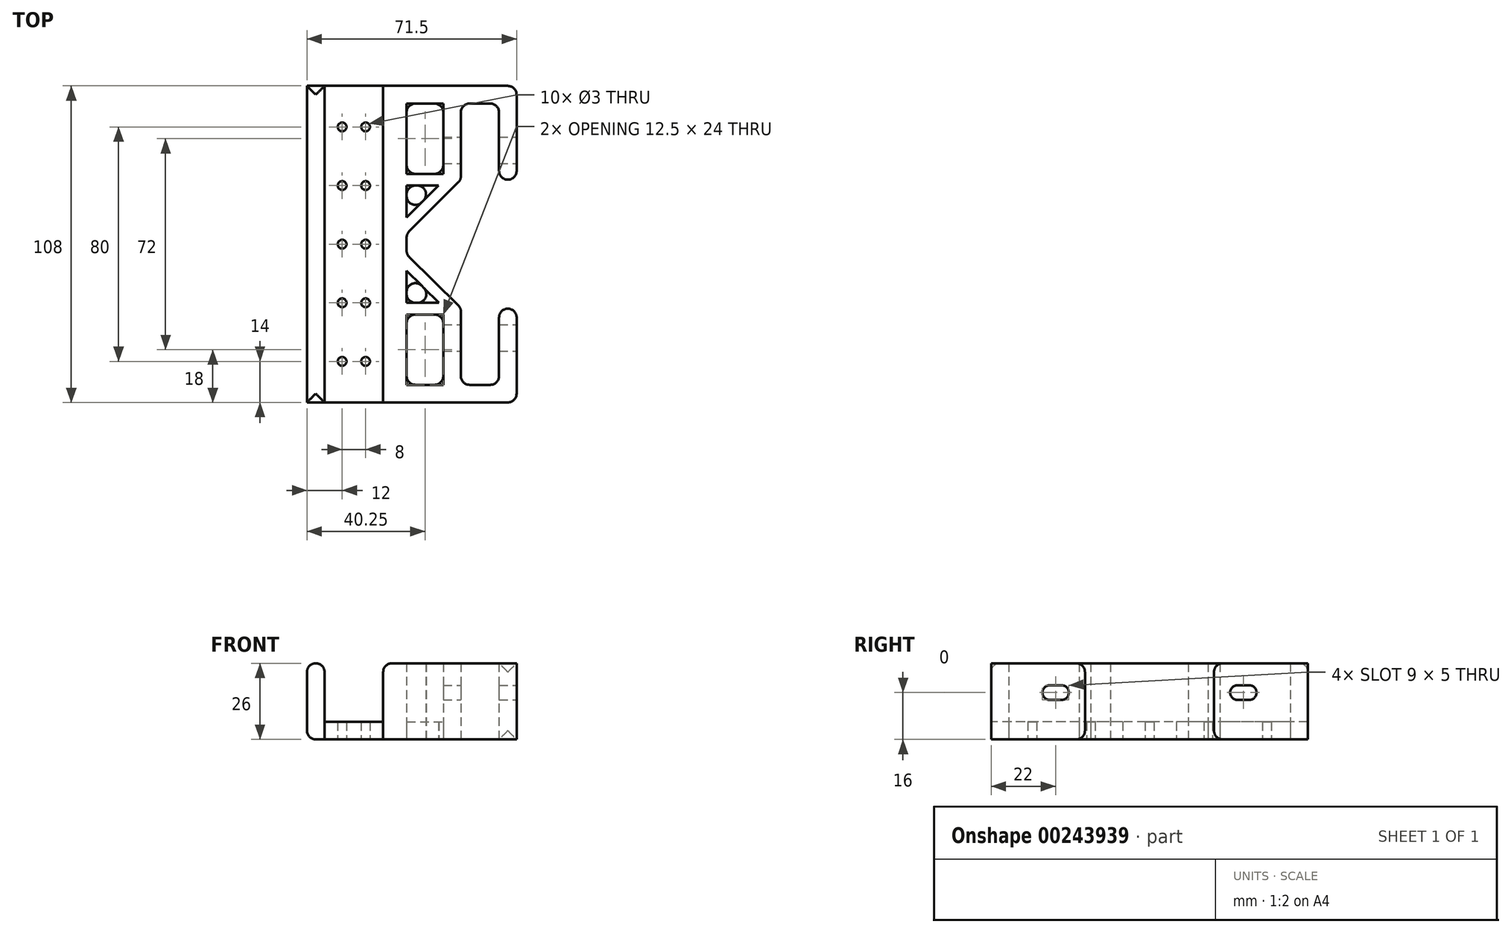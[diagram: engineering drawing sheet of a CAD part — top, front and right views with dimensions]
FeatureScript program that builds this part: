
annotation { "Feature Type Name" : "Feature", "Feature Type Description" : "" }
export const myFeature = defineFeature(function(context is Context, id is Id, definition is map)
    precondition{}
    {
        {
            var Q0;
            Q0=qCreatedBy(makeId("Top.planeOp"),FACE);
            var sketch = newSketch(context, id + "F0", { "sketchPlane" : qUnion([Q0])});
            skLineSegment(sketch, "E0", {"start": v(0, 0) * mm, "end": v(50, 0) * mm, "construction": true});
            skLineSegment(sketch, "E1.0", {"start": v(0, -30) * mm, "end": v(50, -30) * mm, "construction": true});
            skLineSegment(sketch, "E2.0", {"start": v(0, 30) * mm, "end": v(50, 30) * mm, "construction": true});
            skLineSegment(sketch, "E3", {"start": v(0, 48) * mm, "end": v(0, 24) * mm});
            skLineSegment(sketch, "E4.0", {"start": v(25, 30) * mm, "end": v(25, -30) * mm, "construction": true});
            skLineSegment(sketch, "E5.0", {"start": v(0, -48) * mm, "end": v(12.5, -48) * mm});
            skLineSegment(sketch, "E6.0", {"start": v(0, 48) * mm, "end": v(12.5, 48) * mm});
            skLineSegment(sketch, "E7.0", {"start": v(18.5, 48) * mm, "end": v(18.5, 22) * mm});
            skLineSegment(sketch, "E8.0", {"start": v(31.5, 48) * mm, "end": v(31.5, 22) * mm});
            skLineSegment(sketch, "E9.trimOffspring", {"start": v(18.5, -21.75) * mm, "end": v(18.5, -48) * mm});
            skLineSegment(sketch, "E10.trimOffspring", {"start": v(31.5, -22) * mm, "end": v(31.5, -48) * mm});
            skLineSegment(sketch, "E11", {"start": v(25, 21) * mm, "end": v(4, 0) * mm, "construction": true});
            skLineSegment(sketch, "E12", {"start": v(25, -21) * mm, "end": v(4, 0) * mm, "construction": true});
            skLineSegment(sketch, "E13", {"start": v(25, -21) * mm, "end": v(46, 0) * mm, "construction": true});
            skLineSegment(sketch, "E14", {"start": v(46, 0) * mm, "end": v(25, 21) * mm, "construction": true});
            skLineSegment(sketch, "E15.trimOffspring", {"start": v(31.5, 22) * mm, "end": v(37.5, 22) * mm});
            skLineSegment(sketch, "E16.trimOffspring", {"start": v(31.5, -22) * mm, "end": v(37.5, -22) * mm});
            skLineSegment(sketch, "E17", {"start": v(0, 3.5) * mm, "end": v(18.5, 22) * mm});
            skLineSegment(sketch, "E18", {"start": v(0, -3.5) * mm, "end": v(18.5, -21.75) * mm});
            skLineSegment(sketch, "E19.0", {"start": v(37.5, -22) * mm, "end": v(37.5, -54) * mm});
            skLineSegment(sketch, "E20.0", {"start": v(-34, -54) * mm, "end": v(37.5, -54) * mm});
            skLineSegment(sketch, "E21.0", {"start": v(37.5, 54) * mm, "end": v(37.5, 22) * mm});
            skLineSegment(sketch, "E22.0", {"start": v(-34, 54) * mm, "end": v(37.5, 54) * mm});
            skLineSegment(sketch, "E23.0", {"start": v(-8, 54) * mm, "end": v(-8, -54) * mm});
            skLineSegment(sketch, "E24.0", {"start": v(12.5, 48) * mm, "end": v(12.5, 24) * mm});
            skLineSegment(sketch, "E25.0", {"start": v(12.5, -24) * mm, "end": v(12.5, -48) * mm});
            skLineSegment(sketch, "E26.0", {"start": v(0, -9.12) * mm, "end": v(11.03, -20) * mm});
            skLineSegment(sketch, "E27.0", {"start": v(0, 9.16) * mm, "end": v(10.84, 20) * mm});
            skLineSegment(sketch, "E28.trimOffspring", {"start": v(18.5, 48) * mm, "end": v(31.5, 48) * mm});
            skLineSegment(sketch, "E29.trimOffspring", {"start": v(18.5, -48) * mm, "end": v(31.5, -48) * mm});
            skLineSegment(sketch, "E30.0", {"start": v(0, 20) * mm, "end": v(10.84, 20) * mm});
            skLineSegment(sketch, "E31.0", {"start": v(0, 24) * mm, "end": v(12.5, 24) * mm});
            skLineSegment(sketch, "E32.0", {"start": v(0, -20) * mm, "end": v(11.03, -20) * mm});
            skLineSegment(sketch, "E33.0", {"start": v(0, -24) * mm, "end": v(12.5, -24) * mm});
            skLineSegment(sketch, "E34.trimOffspring", {"start": v(0, 20) * mm, "end": v(0, 9.16) * mm});
            skLineSegment(sketch, "E35.trimOffspring", {"start": v(0, -24) * mm, "end": v(0, -48) * mm});
            skLineSegment(sketch, "E36.trimOffspring", {"start": v(0, 3.5) * mm, "end": v(0, -3.5) * mm});
            skLineSegment(sketch, "E37.trimOffspring", {"start": v(0, -9.12) * mm, "end": v(0, -20) * mm});
            skLineSegment(sketch, "E38.0", {"start": v(-28, 54) * mm, "end": v(-28, -54) * mm});
            skLineSegment(sketch, "E39.0", {"start": v(-34, 54) * mm, "end": v(-34, -54) * mm});
            skLineSegment(sketch, "E40.0", {"start": v(-28, 0) * mm, "end": v(-8, 0) * mm, "construction": true});
            skLineSegment(sketch, "E41.0", {"start": v(-14, 54) * mm, "end": v(-14, 40) * mm, "construction": true});
            skCircle(sketch, "E42", {"center": v(-22, 40) * mm, "radius": 1.5 * mm});
            skCircle(sketch, "E43", {"center": v(-14, 40) * mm, "radius": 1.5 * mm});
            skCircle(sketch, "E44", {"center": v(-22, 20) * mm, "radius": 1.5 * mm});
            skCircle(sketch, "E45", {"center": v(-14, 20) * mm, "radius": 1.5 * mm});
            skCircle(sketch, "E46", {"center": v(-22, 0) * mm, "radius": 1.5 * mm});
            skCircle(sketch, "E47", {"center": v(-14, 0) * mm, "radius": 1.5 * mm});
            skCircle(sketch, "E48", {"center": v(-22, -20) * mm, "radius": 1.5 * mm});
            skCircle(sketch, "E49", {"center": v(-14, -20) * mm, "radius": 1.5 * mm});
            skCircle(sketch, "E50", {"center": v(-22, -40) * mm, "radius": 1.5 * mm});
            skCircle(sketch, "E51", {"center": v(-14, -40) * mm, "radius": 1.5 * mm});
            skSolve(sketch);
        }
        {
            var Q0;
            Q0=makeQuery(id+"F0.imprint","IMPRINT",FACE,{"disambiguationData":[TD([[makeQuery(id+"F0.imprint","IMPRINT",EDGE,{"derivedFrom":sQuery(id+"F0.wireOp",EDGE,"E5.0")}),1.0]])]});
            var Q1;
            Q1=makeQuery(id+"F0.imprint","IMPRINT",FACE,{"disambiguationData":[TD([[makeQuery(id+"F0.imprint","IMPRINT",EDGE,{"derivedFrom":sQuery(id+"F0.wireOp",EDGE,"E26.0")}),-1.0]])]});
            var Q2;
            Q2=makeQuery(id+"F0.imprint","IMPRINT",FACE,{"disambiguationData":[TD([[makeQuery(id+"F0.imprint","IMPRINT",EDGE,{"derivedFrom":sQuery(id+"F0.wireOp",EDGE,"E3")}),1.0]])]});
            var Q3;
            {var subQ0=sQuery(id+"F0.wireOp",EDGE,"E23.0");Q3=makeQuery(id+"F0.imprint","IMPRINT",FACE,{"disambiguationData":[TD([[makeQuery(id+"F0.imprint","IMPRINT",EDGE,{"derivedFrom":subQ0}),-1.0]])]});}
            var Q4;
            Q4=makeQuery(id+"F0.imprint","IMPRINT",FACE,{"disambiguationData":[TD([[makeQuery(id+"F0.imprint","IMPRINT",EDGE,{"derivedFrom":sQuery(id+"F0.wireOp",EDGE,"E27.0")}),1.0]])]});
            extrude(context, id + "F1", {"entities" : qUnion([Q0, Q1, Q2, Q3, Q4]), "depth" : 6 * mm});
        }
        {
            var Q0;
            Q0=makeQuery(id+"F0.imprint","IMPRINT",FACE,{"disambiguationData":[TD([[makeQuery(id+"F0.imprint","IMPRINT",EDGE,{"derivedFrom":sQuery(id+"F0.wireOp",EDGE,"E3")}),-1.0]])]});
            var Q1;
            {var subQ2=sQuery(id+"F0.wireOp",EDGE,"E38.0");Q1=makeQuery(id+"F0.imprint","IMPRINT",FACE,{"disambiguationData":[TD([[makeQuery(id+"F0.imprint","IMPRINT",EDGE,{"derivedFrom":subQ2}),-1.0]])]});}
            extrude(context, id + "F2", {"entities" : qUnion([Q0, Q1]), "depth" : 26 * mm});
        }
        {
            var Q0;
            Q0=qCreatedBy(makeId("Right.planeOp"),FACE);
            cPlane(context, id + "F3", {"entities" : qUnion([Q0]), "cplaneType" : CPlaneType.OFFSET, "offset" : 37.5 * mm, "width" : 150 * mm, "height" : 150 * mm});
        }
        {
            var Q0;
            Q0=qCreatedBy(id+"F3.planeOp",FACE);
            var sketch = newSketch(context, id + "F4", { "sketchPlane" : qUnion([Q0])});
            skLineSegment(sketch, "E52", {"start": v(-75.22, 0) * mm, "end": v(74.78, 0) * mm, "construction": true});
            skLineSegment(sketch, "E53", {"start": v(0, 0) * mm, "end": v(0, 50) * mm, "construction": true});
            skLineSegment(sketch, "E54.0", {"start": v(30, 13.5) * mm, "end": v(30, 18.5) * mm, "construction": true});
            skLineSegment(sketch, "E55.0", {"start": v(-30, 13.5) * mm, "end": v(-30, 18.5) * mm, "construction": true});
            skLineSegment(sketch, "E56.0", {"start": v(-75.22, 16) * mm, "end": v(-34, 16) * mm, "construction": true});
            skLineSegment(sketch, "E57.0", {"start": v(34, 13.5) * mm, "end": v(34, 18.5) * mm, "construction": true});
            skLineSegment(sketch, "E58.0", {"start": v(-34, 13.5) * mm, "end": v(-34, 18.5) * mm, "construction": true});
            skLineSegment(sketch, "E59.0", {"start": v(-34, 13.5) * mm, "end": v(-30, 13.5) * mm});
            skLineSegment(sketch, "E60.0", {"start": v(-34, 18.5) * mm, "end": v(-30, 18.5) * mm});
            skLineSegment(sketch, "E61.trimOffspring", {"start": v(-30, 16) * mm, "end": v(30, 16) * mm, "construction": true});
            skLineSegment(sketch, "E62.trimOffspring", {"start": v(34, 16) * mm, "end": v(74.78, 16) * mm, "construction": true});
            skArc(sketch, "E63", {"start": v(-34, 18.5) * mm, "mid": v(-36.5, 16) * mm, "end": v(-34, 13.5) * mm});
            skArc(sketch, "E64", {"start": v(-30, 13.5) * mm, "mid": v(-27.5, 16) * mm, "end": v(-30, 18.5) * mm});
            skArc(sketch, "E65", {"start": v(30, 18.5) * mm, "mid": v(27.5, 16) * mm, "end": v(30, 13.5) * mm});
            skArc(sketch, "E66", {"start": v(34, 13.5) * mm, "mid": v(36.5, 16) * mm, "end": v(34, 18.5) * mm});
            skLineSegment(sketch, "E67.trimOffspring", {"start": v(30, 13.5) * mm, "end": v(34, 13.5) * mm});
            skLineSegment(sketch, "E68.trimOffspring", {"start": v(30, 18.5) * mm, "end": v(34, 18.5) * mm});
            skSolve(sketch);
        }
        {
            var Q0;
            Q0=makeQuery(id+"F4.imprint","IMPRINT",FACE,{"disambiguationData":[TD([[makeQuery(id+"F4.imprint","IMPRINT",EDGE,{"derivedFrom":sQuery(id+"F4.wireOp",EDGE,"E59.0")}),1.0]])]});
            var Q1;
            Q1=makeQuery(id+"F4.imprint","IMPRINT",FACE,{"disambiguationData":[TD([[makeQuery(id+"F4.imprint","IMPRINT",EDGE,{"derivedFrom":sQuery(id+"F4.wireOp",EDGE,"E65")}),1.0]])]});
            extrude(context, id + "F5", {"entities" : qUnion([Q0, Q1]), "operationType" : NewBodyOperationType.REMOVE, "oppositeDirection" : true, "depth" : 30 * mm});
        }
        {
            var Q0;
            Q0=makeQuery(id+"F2.opExtrude","SWEPT_EDGE",EDGE,{"disambiguationData":[OSD([sQuery(id+"F0.wireOp",EDGE,"E3"),sQuery(id+"F0.wireOp",EDGE,"E6.0")])]});
            var Q1;
            Q1=makeQuery(id+"F2.opExtrude","SWEPT_EDGE",EDGE,{"disambiguationData":[OSD([sQuery(id+"F0.wireOp",EDGE,"E7.0"),sQuery(id+"F0.wireOp",EDGE,"E28.trimOffspring")])]});
            var Q2;
            Q2=makeQuery(id+"F2.opExtrude","SWEPT_EDGE",EDGE,{"disambiguationData":[OSD([sQuery(id+"F0.wireOp",EDGE,"E8.0"),sQuery(id+"F0.wireOp",EDGE,"E28.trimOffspring")])]});
            var Q3;
            Q3=makeQuery(id+"F2.opExtrude","SWEPT_EDGE",EDGE,{"disambiguationData":[OSD([sQuery(id+"F0.wireOp",EDGE,"E6.0"),sQuery(id+"F0.wireOp",EDGE,"E24.0")])]});
            var Q4;
            Q4=makeQuery(id+"F2.opExtrude","SWEPT_EDGE",EDGE,{"disambiguationData":[OSD([sQuery(id+"F0.wireOp",EDGE,"E25.0"),sQuery(id+"F0.wireOp",EDGE,"E33.0")])]});
            var Q5;
            Q5=makeQuery(id+"F2.opExtrude","SWEPT_EDGE",EDGE,{"disambiguationData":[OSD([sQuery(id+"F0.wireOp",EDGE,"E33.0"),sQuery(id+"F0.wireOp",EDGE,"E35.trimOffspring")])]});
            var Q6;
            Q6=makeQuery(id+"F2.opExtrude","SWEPT_EDGE",EDGE,{"disambiguationData":[OSD([sQuery(id+"F0.wireOp",EDGE,"E30.0"),sQuery(id+"F0.wireOp",EDGE,"E34.trimOffspring")])]});
            var Q7;
            Q7=makeQuery(id+"F2.opExtrude","SWEPT_EDGE",EDGE,{"disambiguationData":[OSD([sQuery(id+"F0.wireOp",EDGE,"E26.0"),sQuery(id+"F0.wireOp",EDGE,"E37.trimOffspring")])]});
            var Q8;
            Q8=makeQuery(id+"F2.opExtrude","SWEPT_EDGE",EDGE,{"disambiguationData":[OSD([sQuery(id+"F0.wireOp",EDGE,"E32.0"),sQuery(id+"F0.wireOp",EDGE,"E37.trimOffspring")])]});
            var Q9;
            Q9=makeQuery(id+"F2.opExtrude","SWEPT_EDGE",EDGE,{"disambiguationData":[OSD([sQuery(id+"F0.wireOp",EDGE,"E26.0"),sQuery(id+"F0.wireOp",EDGE,"E32.0")])]});
            var Q10;
            Q10=makeQuery(id+"F2.opExtrude","SWEPT_EDGE",EDGE,{"disambiguationData":[OSD([sQuery(id+"F0.wireOp",EDGE,"E27.0"),sQuery(id+"F0.wireOp",EDGE,"E30.0")])]});
            var Q11;
            Q11=makeQuery(id+"F2.opExtrude","SWEPT_EDGE",EDGE,{"disambiguationData":[OSD([sQuery(id+"F0.wireOp",EDGE,"E27.0"),sQuery(id+"F0.wireOp",EDGE,"E34.trimOffspring")])]});
            var Q12;
            Q12=makeQuery(id+"F2.opExtrude","SWEPT_EDGE",EDGE,{"disambiguationData":[OSD([sQuery(id+"F0.wireOp",EDGE,"E5.0"),sQuery(id+"F0.wireOp",EDGE,"E35.trimOffspring")])]});
            var Q13;
            Q13=makeQuery(id+"F2.opExtrude","SWEPT_EDGE",EDGE,{"disambiguationData":[OSD([sQuery(id+"F0.wireOp",EDGE,"E9.trimOffspring"),sQuery(id+"F0.wireOp",EDGE,"E29.trimOffspring")])]});
            var Q14;
            Q14=makeQuery(id+"F2.opExtrude","SWEPT_EDGE",EDGE,{"disambiguationData":[OSD([sQuery(id+"F0.wireOp",EDGE,"E3"),sQuery(id+"F0.wireOp",EDGE,"E31.0")])]});
            var Q15;
            Q15=makeQuery(id+"F2.opExtrude","SWEPT_EDGE",EDGE,{"disambiguationData":[OSD([sQuery(id+"F0.wireOp",EDGE,"E24.0"),sQuery(id+"F0.wireOp",EDGE,"E31.0")])]});
            var Q16;
            Q16=makeQuery(id+"F2.opExtrude","SWEPT_EDGE",EDGE,{"disambiguationData":[OSD([sQuery(id+"F0.wireOp",EDGE,"E5.0"),sQuery(id+"F0.wireOp",EDGE,"E25.0")])]});
            var Q17;
            Q17=makeQuery(id+"F2.opExtrude","SWEPT_EDGE",EDGE,{"disambiguationData":[OSD([sQuery(id+"F0.wireOp",EDGE,"E10.trimOffspring"),sQuery(id+"F0.wireOp",EDGE,"E29.trimOffspring")])]});
            var Q18;
            Q18=makeQuery(id+"F2.opExtrude","SWEPT_EDGE",EDGE,{"disambiguationData":[OSD([sQuery(id+"F0.wireOp",EDGE,"E19.0"),sQuery(id+"F0.wireOp",EDGE,"E20.0")])]});
            var Q19;
            Q19=makeQuery(id+"F2.opExtrude","SWEPT_EDGE",EDGE,{"disambiguationData":[OSD([sQuery(id+"F0.wireOp",EDGE,"E21.0"),sQuery(id+"F0.wireOp",EDGE,"E22.0")])]});
            var Q20;
            Q20=makeQuery(id+"F2.opExtrude","CAP_EDGE",EDGE,{"disambiguationData":[OSD([sQuery(id+"F0.wireOp",EDGE,"E15.trimOffspring")])],"isStart":false});
            var Q21;
            Q21=makeQuery(id+"F2.opExtrude","CAP_EDGE",EDGE,{"disambiguationData":[OSD([sQuery(id+"F0.wireOp",EDGE,"E16.trimOffspring")])],"isStart":false});
            var Q22;
            Q22=makeQuery(id+"F2.opExtrude","CAP_EDGE",EDGE,{"disambiguationData":[OSD([sQuery(id+"F0.wireOp",EDGE,"E16.trimOffspring")])],"isStart":true});
            var Q23;
            Q23=makeQuery(id+"F2.opExtrude","CAP_EDGE",EDGE,{"disambiguationData":[OSD([sQuery(id+"F0.wireOp",EDGE,"E15.trimOffspring")])],"isStart":true});
            var Q24;
            Q24=makeQuery(id+"F2.opExtrude","SWEPT_EDGE",EDGE,{"disambiguationData":[OSD([sQuery(id+"F0.wireOp",EDGE,"E18"),sQuery(id+"F0.wireOp",EDGE,"E36.trimOffspring")])]});
            var Q25;
            Q25=makeQuery(id+"F2.opExtrude","SWEPT_EDGE",EDGE,{"disambiguationData":[OSD([sQuery(id+"F0.wireOp",EDGE,"E17"),sQuery(id+"F0.wireOp",EDGE,"E36.trimOffspring")])]});
            var Q26;
            Q26=makeQuery(id+"F2.opExtrude","SWEPT_EDGE",EDGE,{"disambiguationData":[OSD([sQuery(id+"F0.wireOp",EDGE,"E9.trimOffspring"),sQuery(id+"F0.wireOp",EDGE,"E18")])]});
            var Q27;
            Q27=makeQuery(id+"F2.opExtrude","SWEPT_EDGE",EDGE,{"disambiguationData":[OSD([sQuery(id+"F0.wireOp",EDGE,"E7.0"),sQuery(id+"F0.wireOp",EDGE,"E17")])]});
            var Q28;
            Q28=makeQuery(id+"F2.opExtrude","SWEPT_EDGE",EDGE,{"disambiguationData":[OSD([sQuery(id+"F0.wireOp",EDGE,"E8.0"),sQuery(id+"F0.wireOp",EDGE,"E15.trimOffspring")])]});
            var Q29;
            Q29=makeQuery(id+"F2.opExtrude","SWEPT_EDGE",EDGE,{"disambiguationData":[OSD([sQuery(id+"F0.wireOp",EDGE,"E15.trimOffspring"),sQuery(id+"F0.wireOp",EDGE,"E21.0")])]});
            var Q30;
            Q30=makeQuery(id+"F2.opExtrude","SWEPT_EDGE",EDGE,{"disambiguationData":[OSD([sQuery(id+"F0.wireOp",EDGE,"E10.trimOffspring"),sQuery(id+"F0.wireOp",EDGE,"E16.trimOffspring")])]});
            var Q31;
            Q31=makeQuery(id+"F2.opExtrude","SWEPT_EDGE",EDGE,{"disambiguationData":[OSD([sQuery(id+"F0.wireOp",EDGE,"E16.trimOffspring"),sQuery(id+"F0.wireOp",EDGE,"E19.0")])]});
            var Q32;
            {var subQ0=sQuery(id+"F0.wireOp",EDGE,"E20.0");Q32=makeQuery(id+"F2.opExtrude","CAP_EDGE",EDGE,{"disambiguationData":[OSD([subQ0]),TDD([makeQuery(id+"F0.imprint","IMPRINT",EDGE,{"disambiguationData":[TD([[makeQuery(id+"F0.imprint","INTERSECT",VERTEX,{"derivedFrom":[subQ0,sQuery(id+"F0.wireOp",EDGE,"E39.0")]}),-1.0]])],"derivedFrom":subQ0})])],"isStart":false});}
            var Q33;
            {var subQ0=sQuery(id+"F0.wireOp",EDGE,"E22.0");Q33=makeQuery(id+"F2.opExtrude","CAP_EDGE",EDGE,{"disambiguationData":[OSD([subQ0]),TDD([makeQuery(id+"F0.imprint","IMPRINT",EDGE,{"disambiguationData":[TD([[makeQuery(id+"F0.imprint","INTERSECT",VERTEX,{"derivedFrom":[subQ0,sQuery(id+"F0.wireOp",EDGE,"E39.0")]}),-1.0]])],"derivedFrom":subQ0})])],"isStart":false});}
            var Q34;
            Q34=makeQuery(id+"F2.opExtrude","CAP_EDGE",EDGE,{"disambiguationData":[OSD([sQuery(id+"F0.wireOp",EDGE,"E39.0")])],"isStart":true});
            var Q35;
            Q35=makeQuery(id+"F2.opExtrude","CAP_EDGE",EDGE,{"disambiguationData":[OSD([sQuery(id+"F0.wireOp",EDGE,"E38.0")])],"isStart":false});
            var Q36;
            Q36=makeQuery(id+"F2.opExtrude","CAP_EDGE",EDGE,{"disambiguationData":[OSD([sQuery(id+"F0.wireOp",EDGE,"E23.0")])],"isStart":false});
            var Q37;
            Q37=makeQuery(id+"F2.opExtrude","CAP_EDGE",EDGE,{"disambiguationData":[OSD([sQuery(id+"F0.wireOp",EDGE,"E39.0")])],"isStart":false});
            fillet(context, id + "F6", {"entities" : qUnion([Q0, Q1, Q2, Q3, Q4, Q5, Q6, Q7, Q8, Q9, Q10, Q11, Q12, Q13, Q14, Q15, Q16, Q17, Q18, Q19, Q20, Q21, Q22, Q23, Q24, Q25, Q26, Q27, Q28, Q29, Q30, Q31, Q32, Q33, Q34, Q35, Q36, Q37]), "radius" : 3 * mm, "tangentPropagation" : true, "allowEdgeOverflow" : false});
        }
    });
